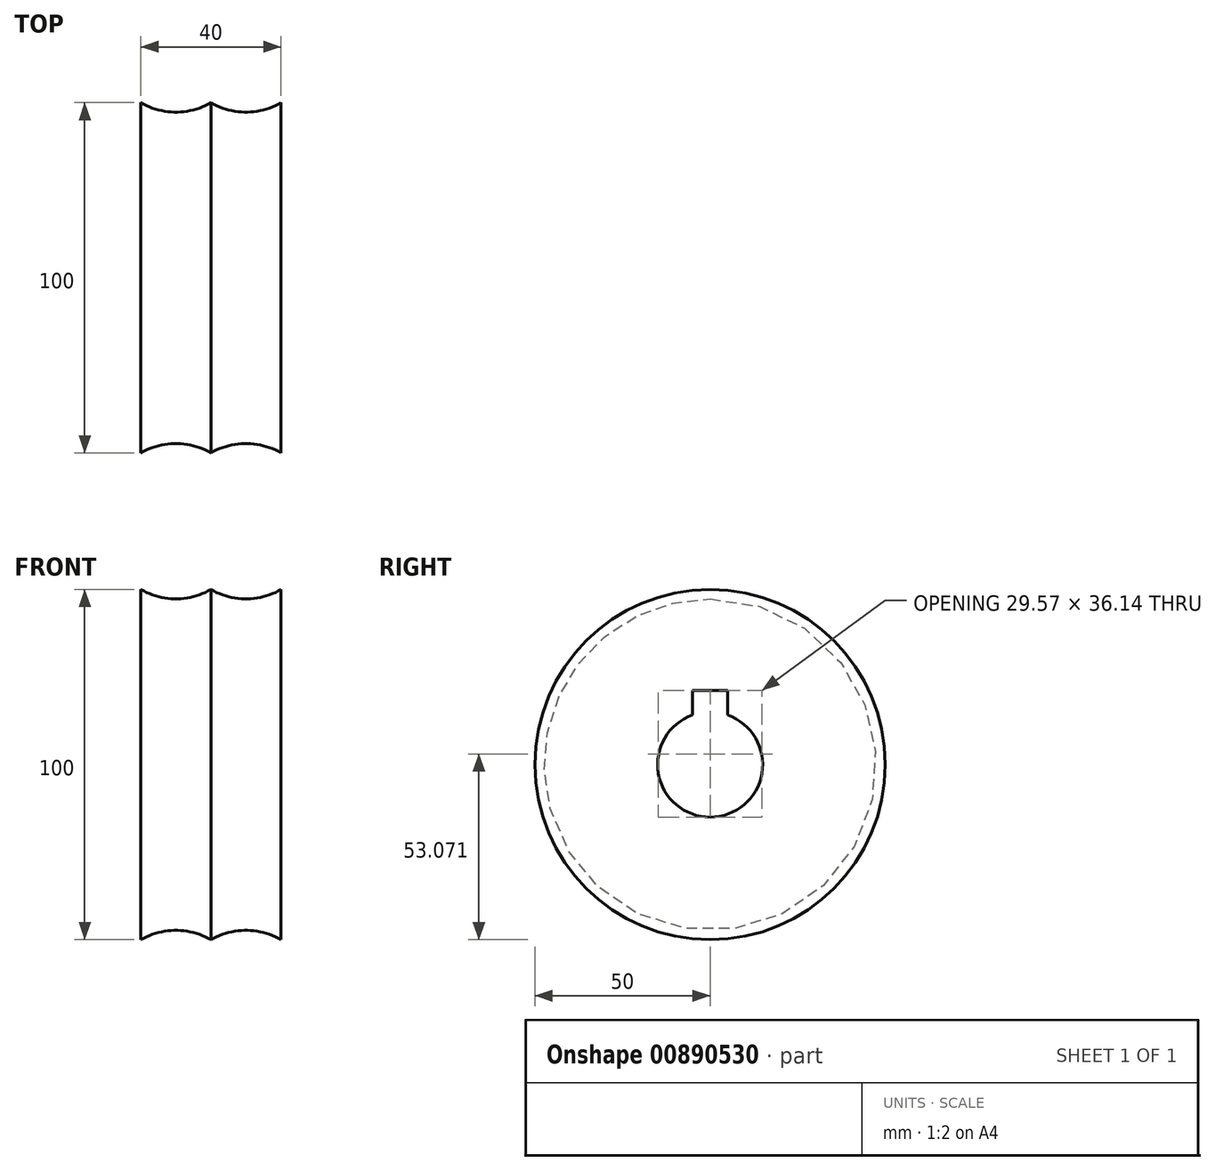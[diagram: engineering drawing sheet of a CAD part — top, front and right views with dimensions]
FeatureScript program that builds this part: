
annotation { "Feature Type Name" : "Feature", "Feature Type Description" : "" }
export const myFeature = defineFeature(function(context is Context, id is Id, definition is map)
    precondition{}
    {
        {
            var Q0;
            Q0=qCreatedBy(makeId("Front.planeOp"),FACE);
            var sketch = newSketch(context, id + "F0", { "sketchPlane" : qUnion([Q0])});
            skLineSegment(sketch, "E0", {"start": v(-20, 0) * mm, "end": v(-20, 50) * mm});
            skArc(sketch, "E1", {"start": v(-20, 50) * mm, "mid": v(-10, 47.32) * mm, "end": v(0, 50) * mm});
            skArc(sketch, "E2.MirrorCS", {"start": v(20, 50) * mm, "mid": v(10, 47.32) * mm, "end": v(0, 50) * mm});
            skLineSegment(sketch, "E3.MirrorCS", {"start": v(20, 0) * mm, "end": v(20, 50) * mm});
            skLineSegment(sketch, "E4", {"start": v(-20, 0) * mm, "end": v(20, 0) * mm});
            skSolve(sketch);
        }
        {
            var Q0;
            Q0 = qSketchRegion(id + "F0", true);
            var Q1;
            Q1=sQuery(id+"F0.wireOp",EDGE,"E4");
            revolve(context, id + "F1", {"surfaceOperationType" : NewSurfaceOperationType.NEW, "entities" : qUnion([Q0]), "axis" : qUnion([Q1]), "revolveType" : RevolveType.FULL});
        }
        {
            var Q0;
            Q0=makeQuery(id+"F1.opRevolve","SWEPT_FACE",FACE,{"disambiguationData":[OSD([sQuery(id+"F0.wireOp",EDGE,"E3.MirrorCS")])]});
            var sketch = newSketch(context, id + "F2", { "sketchPlane" : qUnion([Q0])});
            skArc(sketch, "E5", {"start": v(-5, 14.14) * mm, "mid": v(0, -15) * mm, "end": v(5, 14.14) * mm});
            skLineSegment(sketch, "E6", {"start": v(5, 21.14) * mm, "end": v(5, 14.14) * mm});
            skLineSegment(sketch, "E7.MirrorCS", {"start": v(-5, 21.14) * mm, "end": v(-5, 14.14) * mm});
            skLineSegment(sketch, "E8", {"start": v(-5, 21.14) * mm, "end": v(5, 21.14) * mm});
            skSolve(sketch);
        }
        {
            var Q0;
            {var subQ0=sQuery(id+"F2.wireOp",EDGE,"E5");var subQ1=makeQuery(id+"F2.imprint","INTERSECT",VERTEX,{"derivedFrom":[subQ0,sQuery(id+"F2.wireOp",EDGE,"2d7ppJxf-pNdc-vt1X-zRLg-CPHVwQHxzmgj")]});Q0=makeQuery(id+"F2.imprint","IMPRINT",FACE,{"disambiguationData":[TD([[makeQuery(id+"F2.imprint","IMPRINT",EDGE,{"disambiguationData":[TD([[subQ1,1.0]])],"derivedFrom":subQ0}),1.0]])]});}
            var Q1;
            {var subQ0=sQuery(id+"F2.wireOp",EDGE,"2d7ppJxf-pNdc-vt1X-zRLg-CPHVwQHxzmgj");Q1=makeQuery(id+"F2.imprint","IMPRINT",FACE,{"disambiguationData":[TD([[makeQuery(id+"F2.imprint","IMPRINT",EDGE,{"derivedFrom":subQ0}),-1.0]])]});}
            extrude(context, id + "F3", {"entities" : qUnion([Q0, Q1]), "operationType" : NewBodyOperationType.REMOVE, "oppositeDirection" : true, "depth" : 99990 * mm, "offsetDistance" : 25 * mm});
        }
    });
